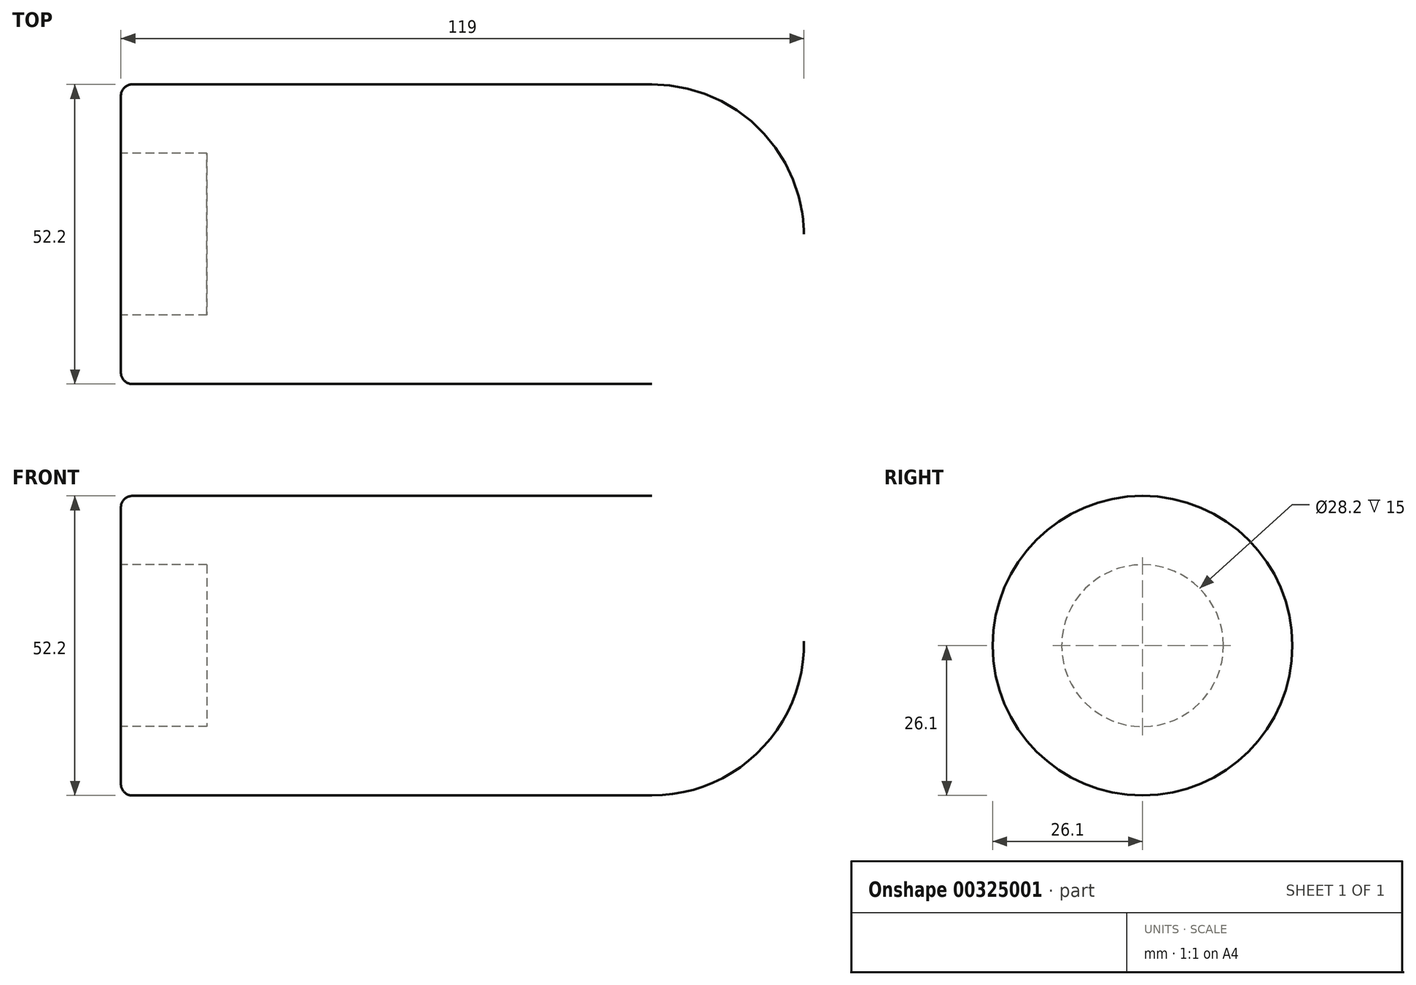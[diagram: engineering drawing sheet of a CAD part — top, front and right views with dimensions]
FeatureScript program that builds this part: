
annotation { "Feature Type Name" : "Feature", "Feature Type Description" : "" }
export const myFeature = defineFeature(function(context is Context, id is Id, definition is map)
    precondition{}
    {
        {
            var Q0;
            Q0=qCreatedBy(makeId("Front.planeOp"),FACE);
            var sketch = newSketch(context, id + "F0", { "sketchPlane" : qUnion([Q0])});
            skLineSegment(sketch, "E0", {"start": v(-74.8, 0) * mm, "end": v(58.4, 0) * mm, "construction": true});
            skLineSegment(sketch, "E1", {"start": v(-45.6, 0) * mm, "end": v(-45.6, 14.1) * mm});
            skLineSegment(sketch, "E2", {"start": v(-45.6, 14.1) * mm, "end": v(-60.6, 14.1) * mm});
            skLineSegment(sketch, "E3", {"start": v(-60.6, 14.1) * mm, "end": v(-60.6, 26.1) * mm});
            skLineSegment(sketch, "E4", {"start": v(-60.6, 26.1) * mm, "end": v(31.9, 26.1) * mm});
            skArc(sketch, "E5", {"start": v(31.9, 26.1) * mm, "mid": v(50.5, 18.48) * mm, "end": v(58.4, 0) * mm});
            skLineSegment(sketch, "E6", {"start": v(-45.6, 0) * mm, "end": v(58.4, 0) * mm});
            skSolve(sketch);
        }
        {
            var Q0;
            Q0 = qSketchRegion(id + "F0", true);
            var Q1;
            Q1=sQuery(id+"F0.wireOp",EDGE,"E0");
            revolve(context, id + "F1", {"entities" : qUnion([Q0]), "axis" : qUnion([Q1]), "revolveType" : RevolveType.FULL});
        }
        {
            var Q0;
            Q0=makeQuery(id+"F1.opRevolve","SWEPT_EDGE",EDGE,{"disambiguationData":[OSD([sQuery(id+"F0.wireOp",EDGE,"E3"),sQuery(id+"F0.wireOp",EDGE,"E4")])]});
            fillet(context, id + "F2", {"entities" : qUnion([Q0]), "radius" : 2 * mm, "tangentPropagation" : true, "allowEdgeOverflow" : false});
        }
    });
